# Revit family: NBS_COBAFlooring_EntMatt_PlanC
name_source: partatom
category: Generic Models
revit_build: Autodesk Revit Architecture 2013 (Build: 20130531_2115(x64)
units: mm (PartAtom-declared; Revit-internal decimal feet)

## types (1)
- PlanC
    Arrangement = Internally inset in a matwell
    AssetType = Fixed
    BIMObjectName = NBS_COBAFlooring_EntranceMatting_PlanC
    BaseColour = Aluminium
    BaseMaterial = 30% recycled aluminium profiles
    CarpetColourOptions = Grey, Black
    Color = Grey, Black
    Combustible = No
    Construction = Open
    Default Elevation = 1200 mm
    Description = Reversible closed surface aluminium entrance matting
    EdgingMaterial = NBS_Concept
    EntranceMattingHeight = 18 mm  [stored 0.0590551 ft]
    EntranceMattingMaterial = NBS_COBAFlooring_Carpet_PlanC
    EntranceMattingWidth = 2000 mm  [stored 6.56168 ft]
    ExpectedLife = 15 years* If used in the correct environment for the volume and type of traffic expected over the system.
    Features = Suitable for heavy-duty use
    Finish = Nylon carpet or rubber strips in an aluminium frame
    FireRating = Bfl-S1
    HasAntiStaticSurface = No
    HasNonSkidSurface = Yes
    IfcExportAs = IfcBuildingElementProxyType
    IfcExportType = USERDEFINED
    IsExternal = No
    LinkingJoints = Aluminium
    ManufacturerName = COBA Flooring
    ManufacturerURL = www.cobaeurope.com/flooring/
    Material = Aluminium frame with Nylon/rubber profile
    MattingHeight = 18 mm
    ModelNumber = Plan C
    ModelReference = Plan C
    NBSCertification = www.nationalbimlibrary.com/cert/qvylnevd
    NBSDescription = Entrance matting
    NBSReference = 45-35-35/420
    Name = EntranceMatting_COBAFlooring_PlanC
    NominalHeight = 18 mm  [stored 0.0590551 ft]
    NominalWidth = 2000 mm  [stored 6.56168 ft]
    Pattern = Horizontal strips
    ProductInformation = www.cobaeurope.com/entrance-matting-systems/plan-c-reversible-aluminium-entrance-matting/
    SurfaceInsertOptions = Grey Nylon filaments, Black Nylon filaments, Black rubber scrapers
    SurfaceInsertWidth = 15 mm
    ThermalTransmittance = 0
    TrafficType = Pedestrian, wheel chairs, pushchairs and trolleys
    Uniclass2 = 45-57-11/426
    Version = 2
    WarrantyStartDate = 1900-12-31T23:59:59

note: [stored X ft] marks values corroborated as IEEE doubles in the binary element streams (Revit-internal decimal feet)

## geometry (parser evidence)
native form markers: Sweep x1
no freeform markers — native parametric forms only
